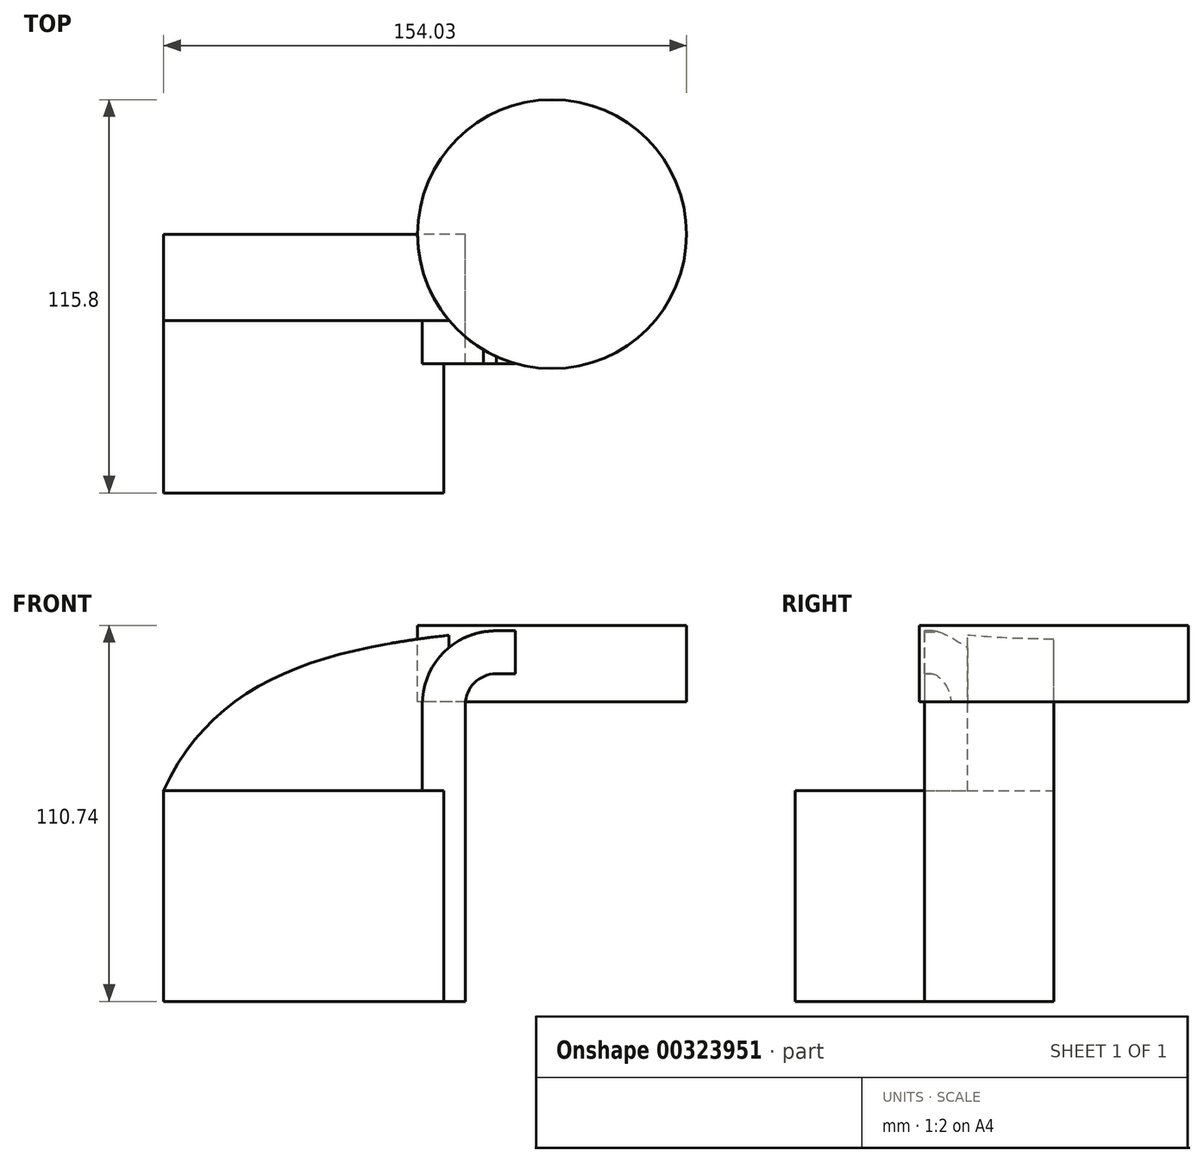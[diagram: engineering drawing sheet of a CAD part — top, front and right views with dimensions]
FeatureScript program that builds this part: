
annotation { "Feature Type Name" : "Feature", "Feature Type Description" : "" }
export const myFeature = defineFeature(function(context is Context, id is Id, definition is map)
    precondition{}
    {
        {
            var Q0;
            Q0=qCreatedBy(makeId("Front.planeOp"),FACE);
            var sketch = newSketch(context, id + "F0", { "sketchPlane" : qUnion([Q0])});
            skLineSegment(sketch, "E0.bottom", {"start": v(44.45, 31) * mm, "end": v(-44.45, 31) * mm});
            skLineSegment(sketch, "E0.top", {"start": v(44.45, -31) * mm, "end": v(-44.45, -31) * mm});
            skLineSegment(sketch, "E0.left", {"start": v(44.45, 31) * mm, "end": v(44.45, -31) * mm});
            skLineSegment(sketch, "E0.right", {"start": v(-44.45, 31) * mm, "end": v(-44.45, -31) * mm});
            skPoint(sketch, "E0.middle", {"position": v(0, 0) * mm});
            skLineSegment(sketch, "E1.bottom", {"start": v(69.99, 79.74) * mm, "end": v(109.58, 79.74) * mm});
            skLineSegment(sketch, "E1.top", {"start": v(69.99, 57.18) * mm, "end": v(109.58, 57.18) * mm});
            skLineSegment(sketch, "E1.left", {"start": v(69.99, 79.74) * mm, "end": v(69.99, 57.18) * mm});
            skLineSegment(sketch, "E1.right", {"start": v(109.58, 79.74) * mm, "end": v(109.58, 57.18) * mm});
            skLineSegment(sketch, "E2", {"start": v(44.45, 31) * mm, "end": v(44.45, 56.4) * mm});
            skArc(sketch, "E3", {"start": v(44.45, 56.4) * mm, "mid": v(47.11, 62.82) * mm, "end": v(53.53, 65.48) * mm});
            skLineSegment(sketch, "E4", {"start": v(53.53, 65.48) * mm, "end": v(79.95, 65.48) * mm});
            skLineSegment(sketch, "E5.0", {"start": v(53.53, 78.18) * mm, "end": v(79.95, 78.18) * mm});
            skArc(sketch, "E5.1", {"start": v(31.75, 56.4) * mm, "mid": v(38.13, 71.8) * mm, "end": v(53.53, 78.18) * mm});
            skLineSegment(sketch, "E5.2", {"start": v(31.75, 31) * mm, "end": v(31.75, 56.4) * mm});
            skLineSegment(sketch, "E6.0", {"start": v(38.1, 31) * mm, "end": v(38.1, -31) * mm});
            skFitSpline(sketch, "E7", {"points": [v(-44.45, 31) * mm, v(53.53, 78.18) * mm], "startDerivative": vector(49.1, 110.03) * mm, "endDerivative": vector(129.8, 11.09) * mm});
            skSolve(sketch);
        }
        {
            var Q0;
            {var subQ0=sQuery(id+"F0.wireOp",EDGE,"E0.right");Q0=makeQuery(id+"F0.imprint","IMPRINT",FACE,{"disambiguationData":[TD([[makeQuery(id+"F0.imprint","IMPRINT",EDGE,{"derivedFrom":subQ0}),1.0]])]});}
            extrude(context, id + "F1", {"entities" : qUnion([Q0]), "depth" : 76.2 * mm});
        }
        {
            var Q0;
            {var subQ0=sQuery(id+"F0.wireOp",EDGE,"E2");Q0=makeQuery(id+"F0.imprint","IMPRINT",FACE,{"disambiguationData":[TD([[makeQuery(id+"F0.imprint","IMPRINT",EDGE,{"derivedFrom":subQ0}),1.0]])]});}
            var Q1;
            {var subQ0=sQuery(id+"F0.wireOp",EDGE,"E0.left");Q1=makeQuery(id+"F0.imprint","IMPRINT",FACE,{"disambiguationData":[TD([[makeQuery(id+"F0.imprint","IMPRINT",EDGE,{"derivedFrom":subQ0}),-1.0]])]});}
            extrude(context, id + "F2", {"entities" : qUnion([Q0, Q1]), "operationType" : NewBodyOperationType.ADD, "depth" : 38.1 * mm});
        }
        {
            var Q0;
            {var subQ3=sQuery(id+"F0.wireOp",EDGE,"E5.2");Q0=makeQuery(id+"F0.imprint","IMPRINT",FACE,{"disambiguationData":[TD([[makeQuery(id+"F0.imprint","IMPRINT",EDGE,{"derivedFrom":subQ3}),1.0]])]});}
            extrude(context, id + "F3", {"entities" : qUnion([Q0]), "operationType" : NewBodyOperationType.ADD, "depth" : 25.4 * mm});
        }
        {
            var Q0;
            {var subQ3=sQuery(id+"F0.wireOp",EDGE,"E1.bottom");Q0=makeQuery(id+"F0.imprint","IMPRINT",FACE,{"disambiguationData":[TD([[makeQuery(id+"F0.imprint","IMPRINT",EDGE,{"derivedFrom":subQ3}),-1.0]])]});}
            var Q1;
            Q1=sQuery(id+"F0.wireOp",EDGE,"E1.left");
            revolve(context, id + "F4", {"operationType" : NewBodyOperationType.ADD, "entities" : qUnion([Q0]), "axis" : qUnion([Q1]), "revolveType" : RevolveType.FULL});
        }
    });
